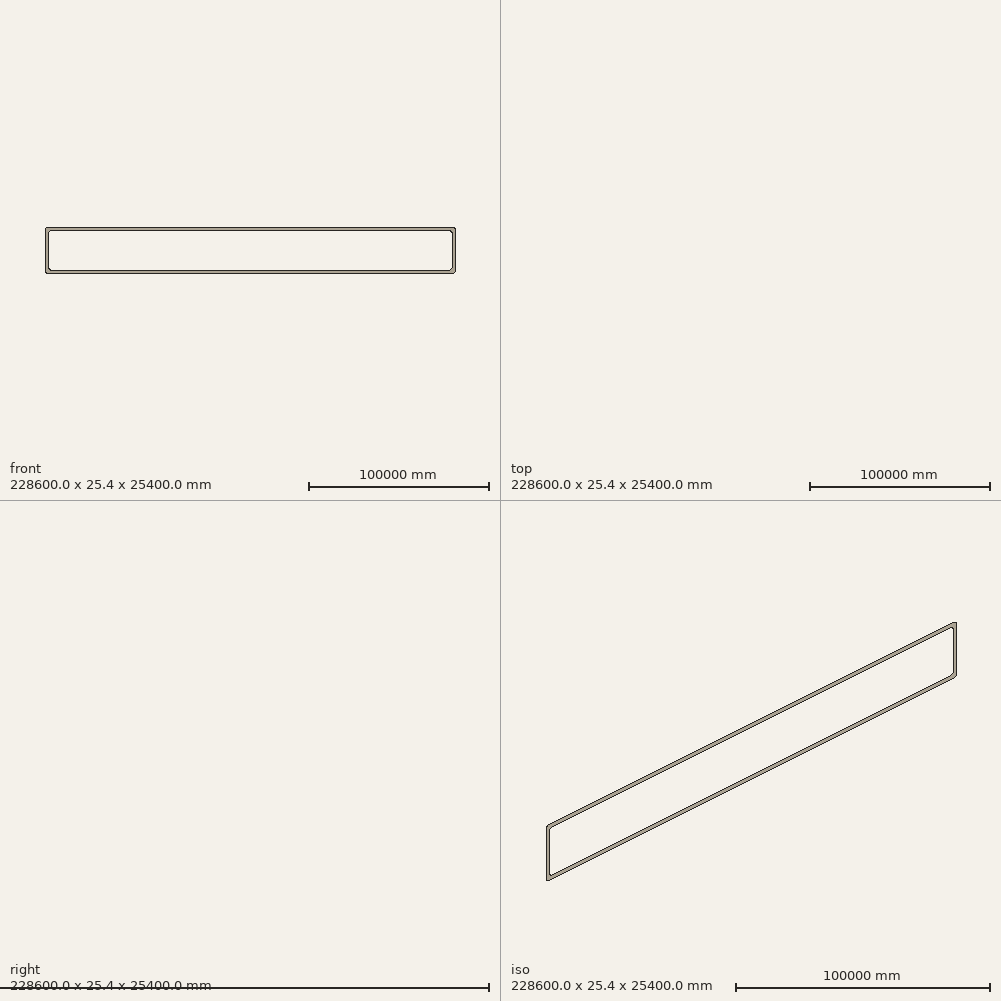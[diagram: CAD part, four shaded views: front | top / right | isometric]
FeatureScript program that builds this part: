
annotation { "Feature Type Name" : "Feature", "Feature Type Description" : "" }
export const myFeature = defineFeature(function(context is Context, id is Id, definition is map)
    precondition{}
    {
        {
            var Q0;
            Q0=qCreatedBy(makeId("Front.planeOp"),FACE);
            var sketch = newSketch(context, id + "F0", { "sketchPlane" : qUnion([Q0])});
            skLineSegment(sketch, "E0.bottom", {"start": v(1270, 0) * mm, "end": v(227330, 0) * mm});
            skLineSegment(sketch, "E0.top", {"start": v(1270, 25400) * mm, "end": v(227330, 25400) * mm});
            skLineSegment(sketch, "E0.left", {"start": v(0, 1270) * mm, "end": v(0, 24130) * mm});
            skLineSegment(sketch, "E0.right", {"start": v(228600, 1270) * mm, "end": v(228600, 24130) * mm});
            skPoint(sketch, "E1.visualSharp", {"position": v(0, 25400) * mm});
            skArc(sketch, "E1.filletArc", {"start": v(1270, 25400) * mm, "mid": v(371.97, 25028.03) * mm, "end": v(0, 24130) * mm});
            skPoint(sketch, "E2.visualSharp", {"position": v(0, 0) * mm});
            skArc(sketch, "E2.filletArc", {"start": v(0, 1270) * mm, "mid": v(371.97, 371.97) * mm, "end": v(1270, 0) * mm});
            skPoint(sketch, "E3.visualSharp", {"position": v(228600, 25400) * mm});
            skArc(sketch, "E3.filletArc", {"start": v(228600, 24130) * mm, "mid": v(228228.03, 25028.03) * mm, "end": v(227330, 25400) * mm});
            skPoint(sketch, "E4.visualSharp", {"position": v(228600, 0) * mm});
            skArc(sketch, "E4.filletArc", {"start": v(227330, 0) * mm, "mid": v(228228.03, 371.97) * mm, "end": v(228600, 1270) * mm});
            skLineSegment(sketch, "E5.0", {"start": v(1778, 3048) * mm, "end": v(1778, 22352) * mm});
            skLineSegment(sketch, "E5.1", {"start": v(3048, 1778) * mm, "end": v(225552, 1778) * mm});
            skLineSegment(sketch, "E5.2", {"start": v(226822, 3048) * mm, "end": v(226822, 22352) * mm});
            skLineSegment(sketch, "E5.3", {"start": v(3048, 23622) * mm, "end": v(225552, 23622) * mm});
            skPoint(sketch, "E6.visualSharp", {"position": v(1778, 23622) * mm});
            skArc(sketch, "E6.filletArc", {"start": v(3048, 23622) * mm, "mid": v(2149.97, 23250.03) * mm, "end": v(1778, 22352) * mm});
            skPoint(sketch, "E7.visualSharp", {"position": v(1778, 1778) * mm});
            skArc(sketch, "E7.filletArc", {"start": v(1778, 3048) * mm, "mid": v(2149.97, 2149.97) * mm, "end": v(3048, 1778) * mm});
            skPoint(sketch, "E8.visualSharp", {"position": v(226822, 1778) * mm});
            skArc(sketch, "E8.filletArc", {"start": v(225552, 1778) * mm, "mid": v(226450.03, 2149.97) * mm, "end": v(226822, 3048) * mm});
            skPoint(sketch, "E9.visualSharp", {"position": v(226822, 23622) * mm});
            skArc(sketch, "E9.filletArc", {"start": v(226822, 22352) * mm, "mid": v(226450.03, 23250.03) * mm, "end": v(225552, 23622) * mm});
            skSolve(sketch);
        }
        {
            var Q0;
            Q0=makeQuery(id+"F0.imprint","IMPRINT",FACE,{"disambiguationData":[TD([[makeQuery(id+"F0.imprint","IMPRINT",EDGE,{"derivedFrom":sQuery(id+"F0.wireOp",EDGE,"E0.bottom")}),1.0]])]});
            extrude(context, id + "F1", {"entities" : qUnion([Q0]), "depth" : 25.4 * mm, "offsetDistance" : 25.4 * mm});
        }
    });
